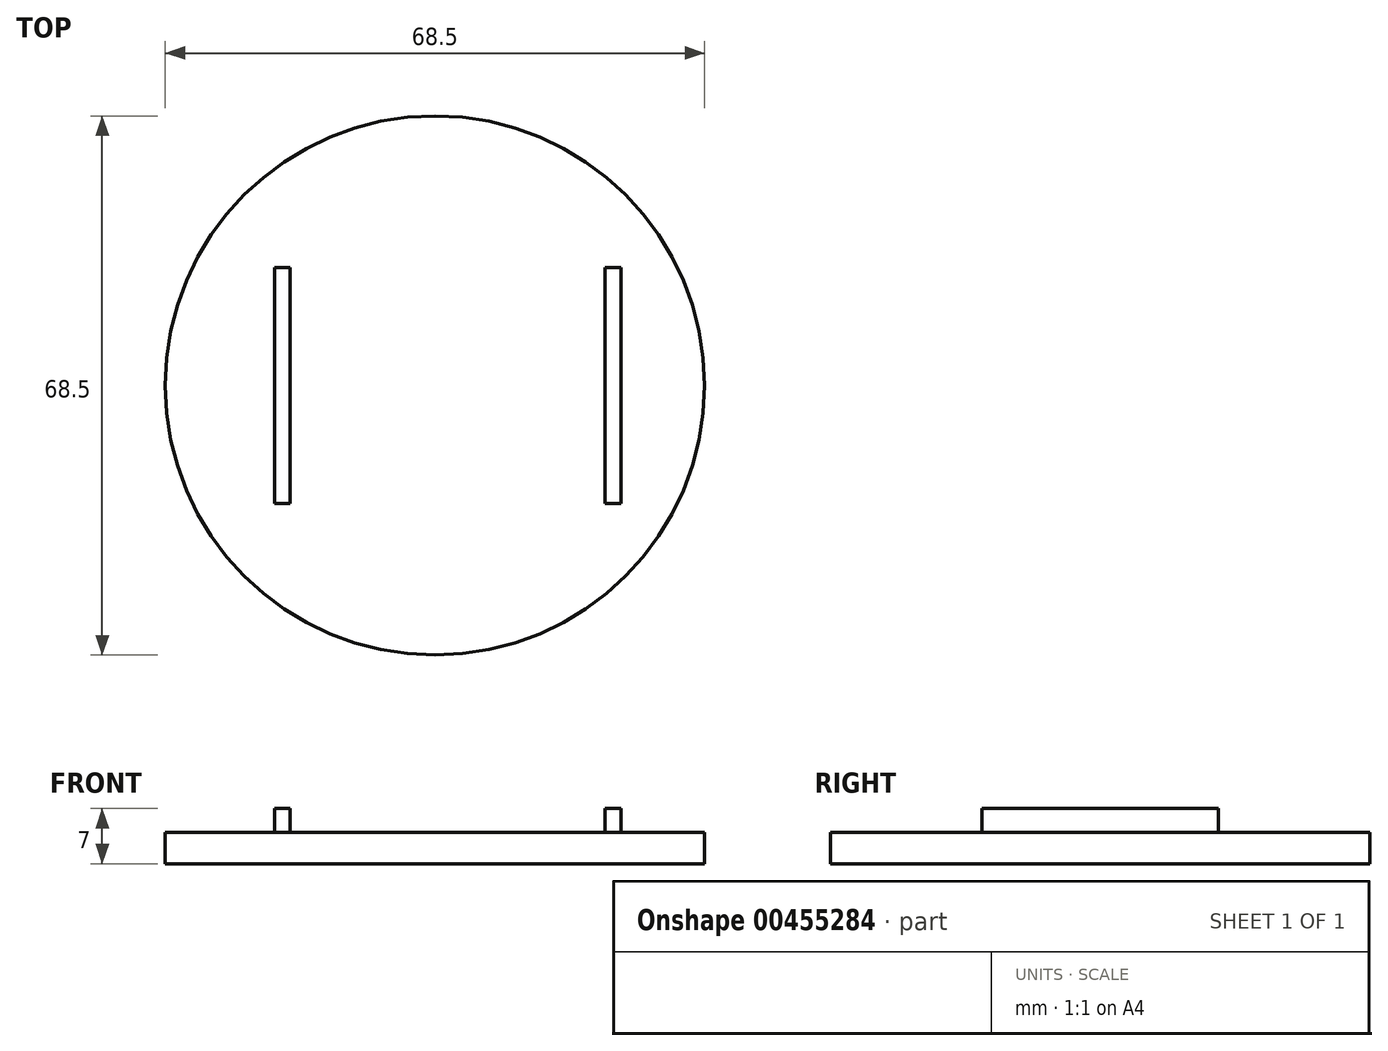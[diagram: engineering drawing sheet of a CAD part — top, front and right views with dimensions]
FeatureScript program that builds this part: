
annotation { "Feature Type Name" : "Feature", "Feature Type Description" : "" }
export const myFeature = defineFeature(function(context is Context, id is Id, definition is map)
    precondition{}
    {
        {
            var Q0;
            Q0=qCreatedBy(makeId("Top.planeOp"),FACE);
            var sketch = newSketch(context, id + "F0", { "sketchPlane" : qUnion([Q0])});
            skCircle(sketch, "E0", {"center": v(0, 0) * mm, "radius": 34.25 * mm});
            skSolve(sketch);
        }
        {
            var Q0;
            Q0 = qSketchRegion(id + "F0", true);
            extrude(context, id + "F1", {"entities" : qUnion([Q0]), "depth" : 4 * mm});
        }
        {
            var Q0;
            Q0=makeQuery(id+"F1.opExtrude","CAP_FACE",FACE,{"disambiguationData":[OSD([sQuery(id+"F0.wireOp",EDGE,"E0")])],"isStart":false});
            var sketch = newSketch(context, id + "F2", { "sketchPlane" : qUnion([Q0])});
            skLineSegment(sketch, "E1", {"start": v(1.62, 0) * mm, "end": v(21.62, 0) * mm});
            skLineSegment(sketch, "E2", {"start": v(21.62, 0) * mm, "end": v(21.62, 15) * mm});
            skLineSegment(sketch, "E3", {"start": v(21.62, 15) * mm, "end": v(23.62, 15) * mm});
            skLineSegment(sketch, "E4", {"start": v(23.62, 15) * mm, "end": v(23.62, -15) * mm});
            skLineSegment(sketch, "E5", {"start": v(23.62, -15) * mm, "end": v(21.62, -15) * mm});
            skLineSegment(sketch, "E6", {"start": v(21.62, -15) * mm, "end": v(21.62, 0) * mm});
            skLineSegment(sketch, "E7", {"start": v(1.62, 0) * mm, "end": v(-18.38, 0) * mm});
            skLineSegment(sketch, "E8", {"start": v(-18.38, 0) * mm, "end": v(-18.38, 15) * mm});
            skLineSegment(sketch, "E9", {"start": v(-18.38, 15) * mm, "end": v(-20.38, 15) * mm});
            skLineSegment(sketch, "E10", {"start": v(-20.38, 15) * mm, "end": v(-20.38, -15) * mm});
            skLineSegment(sketch, "E11", {"start": v(-20.38, -15) * mm, "end": v(-18.38, -15) * mm});
            skLineSegment(sketch, "E12", {"start": v(-18.38, -15) * mm, "end": v(-18.38, 0) * mm});
            skSolve(sketch);
        }
        {
            var Q0;
            Q0 = qSketchRegion(id + "F2", true);
            extrude(context, id + "F3", {"entities" : qUnion([Q0]), "operationType" : NewBodyOperationType.ADD, "depth" : 3 * mm});
        }
    });
